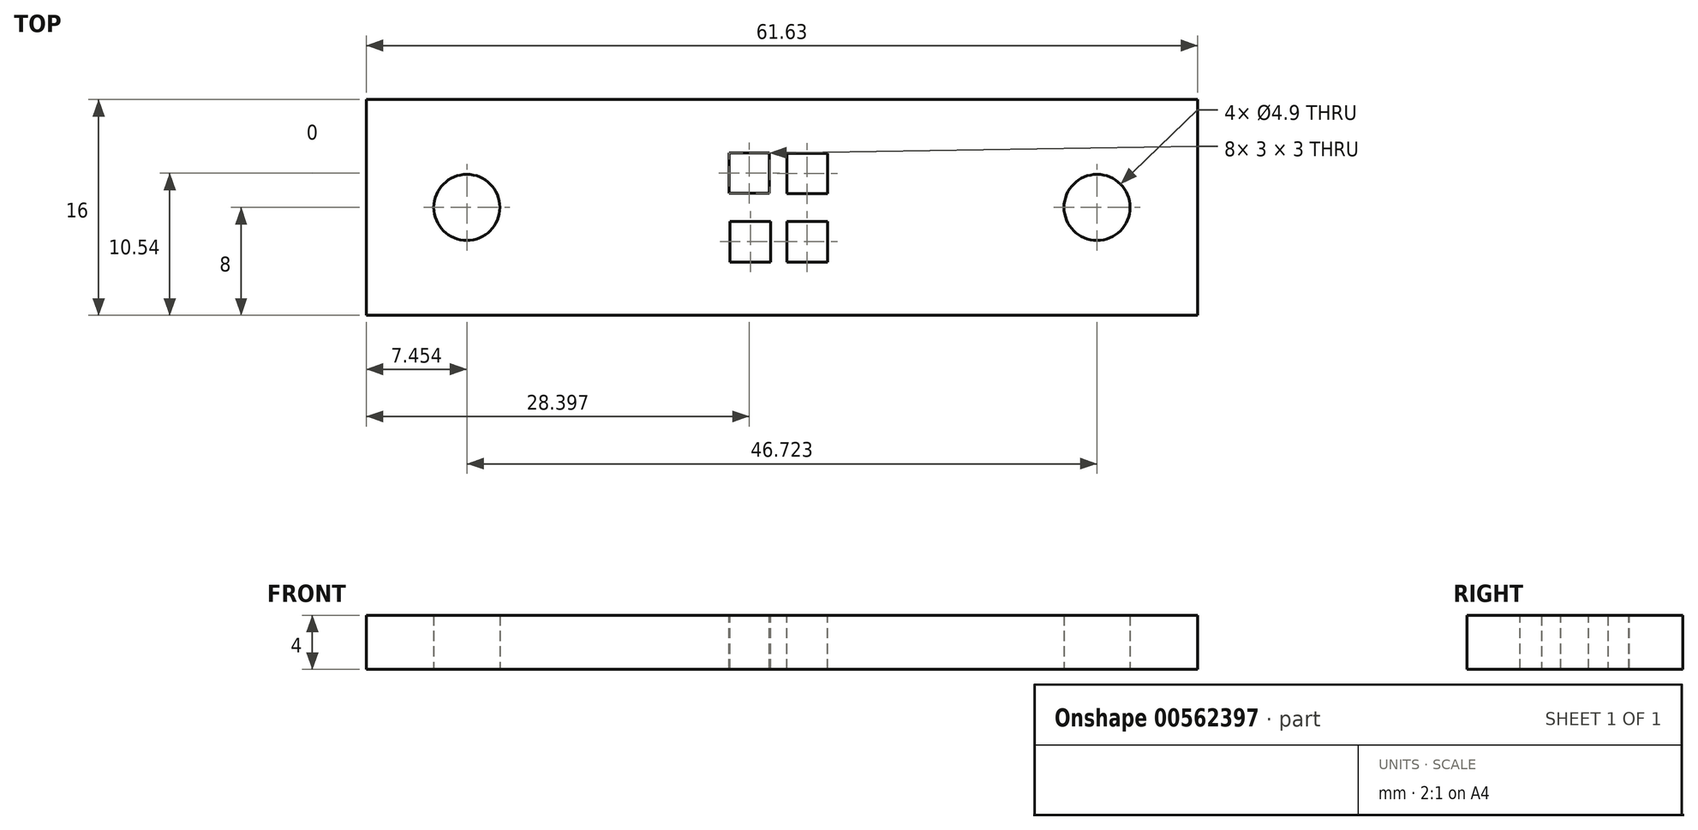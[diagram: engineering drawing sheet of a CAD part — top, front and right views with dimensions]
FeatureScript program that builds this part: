
annotation { "Feature Type Name" : "Feature", "Feature Type Description" : "" }
export const myFeature = defineFeature(function(context is Context, id is Id, definition is map)
    precondition{}
    {
        {
            var Q0;
            Q0=qCreatedBy(makeId("Top.planeOp"),FACE);
            var sketch = newSketch(context, id + "F0", { "sketchPlane" : qUnion([Q0])});
            skLineSegment(sketch, "E0", {"start": v(-8.94, 8) * mm, "end": v(31.07, 8) * mm});
            skLineSegment(sketch, "E1", {"start": v(31.07, 8) * mm, "end": v(31.07, -8) * mm});
            skLineSegment(sketch, "E2", {"start": v(31.07, -8) * mm, "end": v(-8.94, -8) * mm});
            skCircle(sketch, "E3", {"center": v(23.62, 0) * mm, "radius": 2.45 * mm});
            skLineSegment(sketch, "E4", {"start": v(-8.94, -8) * mm, "end": v(-30.56, -8) * mm});
            skLineSegment(sketch, "E5", {"start": v(-30.56, -8) * mm, "end": v(-30.56, 8) * mm});
            skLineSegment(sketch, "E6", {"start": v(-30.56, 8) * mm, "end": v(-8.94, 8) * mm});
            skCircle(sketch, "E7", {"center": v(-23.1, 0) * mm, "radius": 2.45 * mm});
            skSolve(sketch);
        }
        {
            var Q0;
            Q0=qSketchRegion(id+"F0",true);
            extrude(context, id + "F1", {"entities" : qUnion([Q0]), "depth" : 4 * mm, "offsetDistance" : 25 * mm});
        }
        {
            var Q0;
            Q0=makeQuery(id+"F1.opExtrude","CAP_FACE",FACE,{"disambiguationData":[OSD([sQuery(id+"F0.wireOp",EDGE,"E0"),sQuery(id+"F0.wireOp",EDGE,"E1"),sQuery(id+"F0.wireOp",EDGE,"E2"),sQuery(id+"F0.wireOp",EDGE,"E3"),sQuery(id+"F0.wireOp",EDGE,"E4"),sQuery(id+"F0.wireOp",EDGE,"E5"),sQuery(id+"F0.wireOp",EDGE,"E6"),sQuery(id+"F0.wireOp",EDGE,"E7")])],"isStart":false});
            var sketch = newSketch(context, id + "F2", { "sketchPlane" : qUnion([Q0])});
            skLineSegment(sketch, "E8.bottom", {"start": v(-3.66, 4.04) * mm, "end": v(-0.66, 4.04) * mm});
            skLineSegment(sketch, "E8.top", {"start": v(-3.66, 1.04) * mm, "end": v(-0.66, 1.04) * mm});
            skLineSegment(sketch, "E8.left", {"start": v(-3.66, 4.04) * mm, "end": v(-3.66, 1.04) * mm});
            skLineSegment(sketch, "E8.right", {"start": v(-0.66, 4.04) * mm, "end": v(-0.66, 1.04) * mm});
            skLineSegment(sketch, "E9.bottom", {"start": v(0.63, 4.02) * mm, "end": v(3.63, 4.02) * mm});
            skLineSegment(sketch, "E9.top", {"start": v(0.63, 1.02) * mm, "end": v(3.63, 1.02) * mm});
            skLineSegment(sketch, "E9.left", {"start": v(0.63, 4.02) * mm, "end": v(0.63, 1.02) * mm});
            skLineSegment(sketch, "E9.right", {"start": v(3.63, 4.02) * mm, "end": v(3.63, 1.02) * mm});
            skLineSegment(sketch, "E10.bottom", {"start": v(-3.59, -1.04) * mm, "end": v(-0.59, -1.04) * mm});
            skLineSegment(sketch, "E10.top", {"start": v(-3.59, -4.04) * mm, "end": v(-0.59, -4.04) * mm});
            skLineSegment(sketch, "E10.left", {"start": v(-3.59, -1.04) * mm, "end": v(-3.59, -4.04) * mm});
            skLineSegment(sketch, "E10.right", {"start": v(-0.59, -1.04) * mm, "end": v(-0.59, -4.04) * mm});
            skLineSegment(sketch, "E11.bottom", {"start": v(0.63, -1.04) * mm, "end": v(3.63, -1.04) * mm});
            skLineSegment(sketch, "E11.top", {"start": v(0.63, -4.04) * mm, "end": v(3.63, -4.04) * mm});
            skLineSegment(sketch, "E11.left", {"start": v(0.63, -1.04) * mm, "end": v(0.63, -4.04) * mm});
            skLineSegment(sketch, "E11.right", {"start": v(3.63, -1.04) * mm, "end": v(3.63, -4.04) * mm});
            skSolve(sketch);
        }
        {
            var Q0;
            Q0 = qSketchRegion(id + "F2", true);
            extrude(context, id + "F3", {"entities" : qUnion([Q0]), "operationType" : NewBodyOperationType.REMOVE, "endBound" : BoundingType.THROUGH_ALL, "oppositeDirection" : true, "depth" : 25 * mm, "offsetDistance" : 25 * mm});
        }
    });
